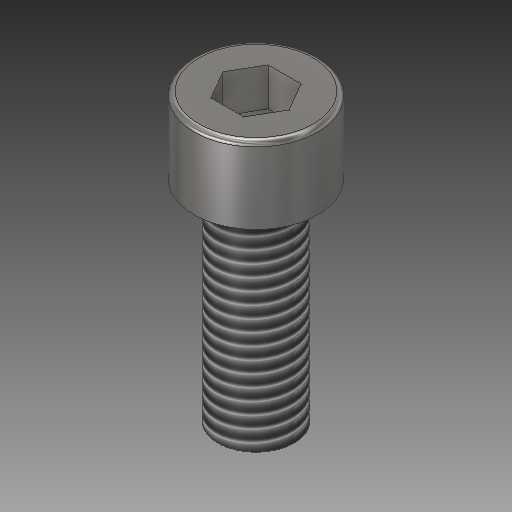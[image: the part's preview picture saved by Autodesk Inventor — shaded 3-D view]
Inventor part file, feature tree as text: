
AUTODESK INVENTOR PART (.ipt)
format: ipt  version: 2019 (Build 230136000, 136)  size: 169,984 bytes
history: native  units: mm
features: other x3, extrude x2, fillet x1
ambient origin geometry x8: Origin, YZ Plane, XZ Plane, XY Plane, X Axis, Y Axis, Z Axis, Center Point
bodies: Solid1 (feature_tree), Body (feature_tree)
feature tree (6):
  extrude  "Cap"  Depth=13.0mm
  extrude  "Key Socket Cutout"  Depth=8.0mm TaperAngle=0.0deg
  fillet  "Cap Fillet"  Radius=6.0mm
  other  "Cap Cross Section"
  other  "Key Socket Cutout Outline"
  other  "Body Cross Section"
